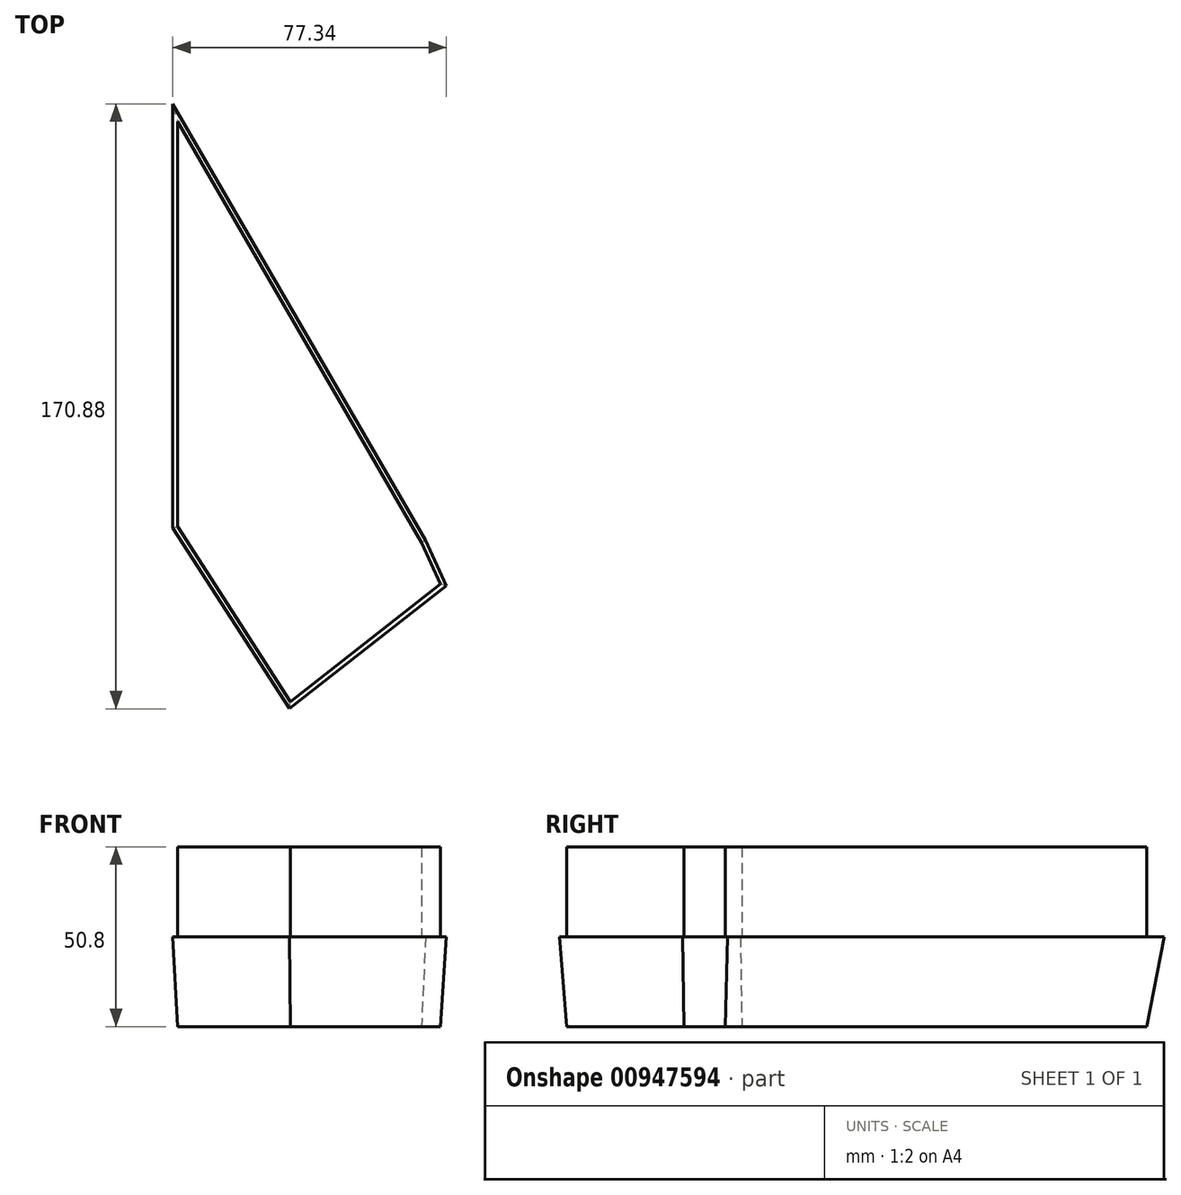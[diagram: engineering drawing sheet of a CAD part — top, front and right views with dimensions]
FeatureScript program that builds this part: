
annotation { "Feature Type Name" : "Feature", "Feature Type Description" : "" }
export const myFeature = defineFeature(function(context is Context, id is Id, definition is map)
    precondition{}
    {
        {
            var Q0;
            Q0=qCreatedBy(makeId("Top.planeOp"),FACE);
            var sketch = newSketch(context, id + "F0", { "sketchPlane" : qUnion([Q0])});
            skLineSegment(sketch, "E0", {"start": v(-46.6, 0) * mm, "end": v(0, 0) * mm});
            skLineSegment(sketch, "E1", {"start": v(0, 0) * mm, "end": v(43.42, 0) * mm});
            skLineSegment(sketch, "E2", {"start": v(43.42, 0) * mm, "end": v(21.71, 0) * mm});
            skLineSegment(sketch, "E3", {"start": v(21.71, 0) * mm, "end": v(27.11, -11.7) * mm});
            skLineSegment(sketch, "E4", {"start": v(27.11, -11.7) * mm, "end": v(-15.28, -44.94) * mm});
            skLineSegment(sketch, "E5", {"start": v(-15.28, -44.94) * mm, "end": v(-47.25, 4.63) * mm});
            skLineSegment(sketch, "E6", {"start": v(-47.25, 4.63) * mm, "end": v(-47.25, 119.04) * mm});
            skLineSegment(sketch, "E7", {"start": v(-47.25, 119.04) * mm, "end": v(21.71, 0) * mm});
            skSolve(sketch);
        }
        {
            var Q0;
            {var subQ1=sQuery(id+"F0.wireOp",EDGE,"E1");Q0=makeQuery(id+"F0.imprint","IMPRINT",FACE,{"disambiguationData":[TD([[makeQuery(id+"F0.imprint","IMPRINT",EDGE,{"derivedFrom":subQ1}),1.0]])]});}
            var Q1;
            {var subQ1=sQuery(id+"F0.wireOp",EDGE,"E1");Q1=makeQuery(id+"F0.imprint","IMPRINT",FACE,{"disambiguationData":[TD([[makeQuery(id+"F0.imprint","IMPRINT",EDGE,{"derivedFrom":subQ1}),-1.0]])]});}
            var Q2;
            Q2 = qSketchRegion(id + "F0", true);
            extrude(context, id + "F1", {"entities" : qUnion([Q0, Q1, Q2]), "depth" : 25.4 * mm, "offsetDistance" : 25.4 * mm, "hasDraft" : true, "draftAngle" : 3 * degree});
        }
        {
            var Q0;
            Q0=makeQuery(id+"F1.opExtrude","CAP_FACE",FACE,{"disambiguationData":[OSD([sQuery(id+"F0.wireOp",EDGE,"E3"),sQuery(id+"F0.wireOp",EDGE,"E4"),sQuery(id+"F0.wireOp",EDGE,"E5"),sQuery(id+"F0.wireOp",EDGE,"E6"),sQuery(id+"F0.wireOp",EDGE,"E7")])],"isStart":true});
            extrude(context, id + "F2", {"entities" : qUnion([Q0]), "operationType" : NewBodyOperationType.ADD, "oppositeDirection" : true, "depth" : 50.8 * mm, "offsetDistance" : 25.4 * mm});
        }
    });
